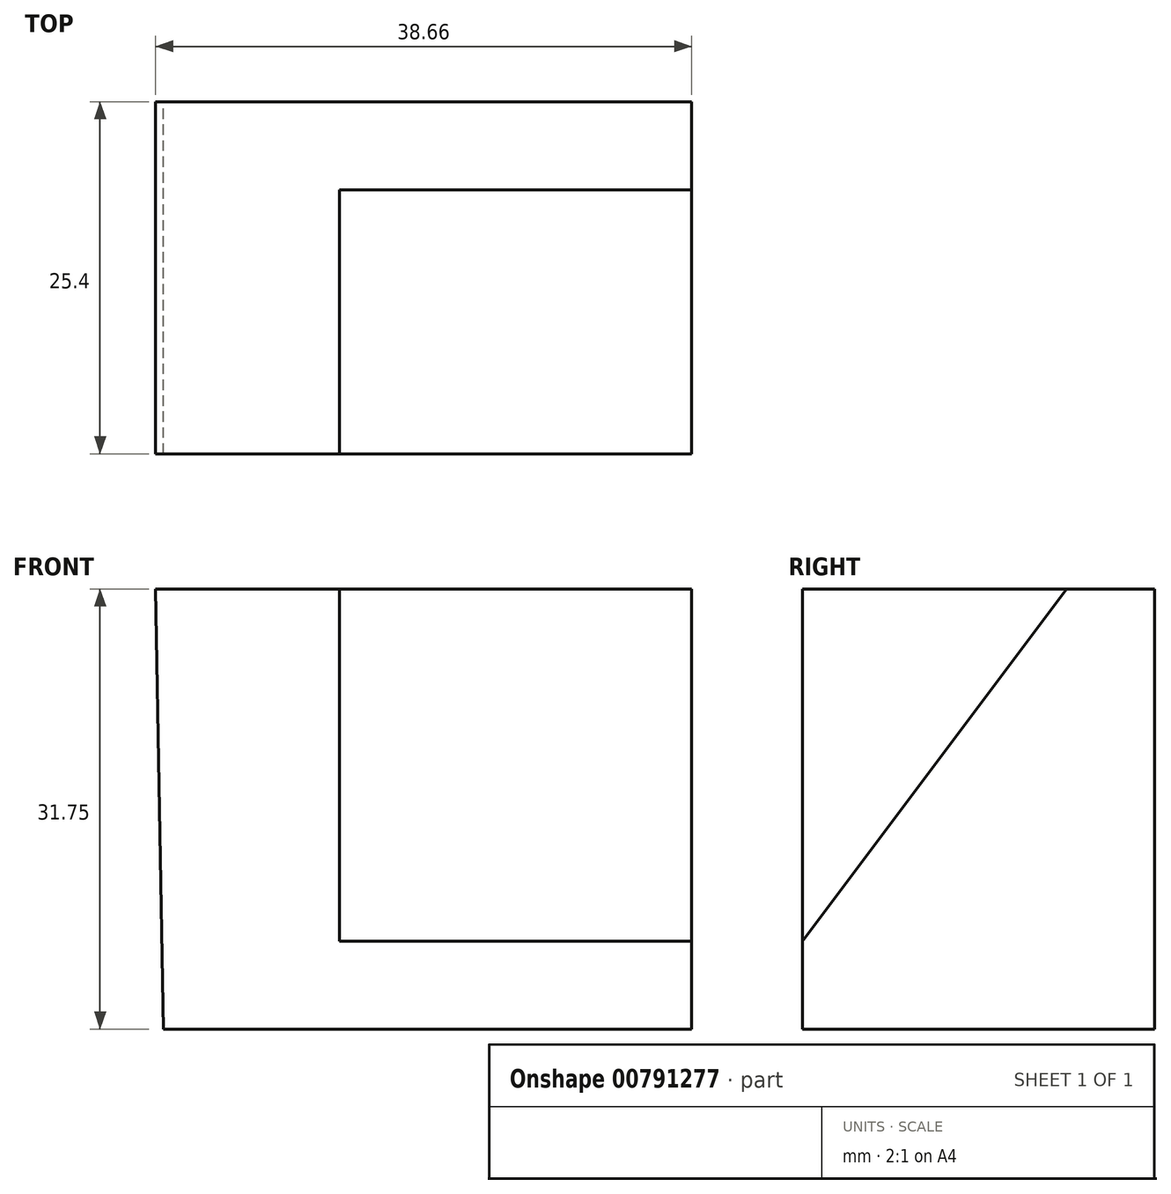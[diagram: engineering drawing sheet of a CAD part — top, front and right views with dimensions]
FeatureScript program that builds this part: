
annotation { "Feature Type Name" : "Feature", "Feature Type Description" : "" }
export const myFeature = defineFeature(function(context is Context, id is Id, definition is map)
    precondition{}
    {
        {
            var Q0;
            Q0=qCreatedBy(makeId("Front.planeOp"),FACE);
            var sketch = newSketch(context, id + "F0", { "sketchPlane" : qUnion([Q0])});
            skLineSegment(sketch, "E0", {"start": v(0, 0) * mm, "end": v(38.1, 0) * mm});
            skLineSegment(sketch, "E1", {"start": v(38.1, 0) * mm, "end": v(38.1, 31.75) * mm});
            skLineSegment(sketch, "E2", {"start": v(38.1, 31.75) * mm, "end": v(-0.56, 31.75) * mm});
            skLineSegment(sketch, "E3", {"start": v(-0.56, 31.75) * mm, "end": v(0, 0) * mm});
            skSolve(sketch);
        }
        {
            var Q0;
            Q0 = qSketchRegion(id + "F0", true);
            extrude(context, id + "F1", {"entities" : qUnion([Q0]), "depth" : 25.4 * mm, "offsetDistance" : 25.4 * mm});
        }
        {
            var Q0;
            Q0=makeQuery(id+"F1.opExtrude","SWEPT_FACE",FACE,{"disambiguationData":[OSD([sQuery(id+"F0.wireOp",EDGE,"E1")])]});
            var sketch = newSketch(context, id + "F2", { "sketchPlane" : qUnion([Q0])});
            skLineSegment(sketch, "E4", {"start": v(-25.4, 0) * mm, "end": v(-25.4, 6.35) * mm, "construction": true});
            skLineSegment(sketch, "E5", {"start": v(0, 31.75) * mm, "end": v(-6.35, 31.75) * mm, "construction": true});
            skLineSegment(sketch, "E6", {"start": v(-6.35, 31.75) * mm, "end": v(-25.4, 6.35) * mm});
            skSolve(sketch);
        }
        {
            var Q0;
            {var subQ0=sQuery(id+"F2.wireOp",EDGE,"E6");Q0=makeQuery(id+"F2.imprint","IMPRINT",FACE,{"disambiguationData":[TD([[makeQuery(id+"F2.imprint","IMPRINT",EDGE,{"derivedFrom":subQ0}),-1.0]])]});}
            extrude(context, id + "F3", {"entities" : qUnion([Q0]), "operationType" : NewBodyOperationType.REMOVE, "oppositeDirection" : true, "depth" : 25.4 * mm, "offsetDistance" : 25.4 * mm});
        }
    });
